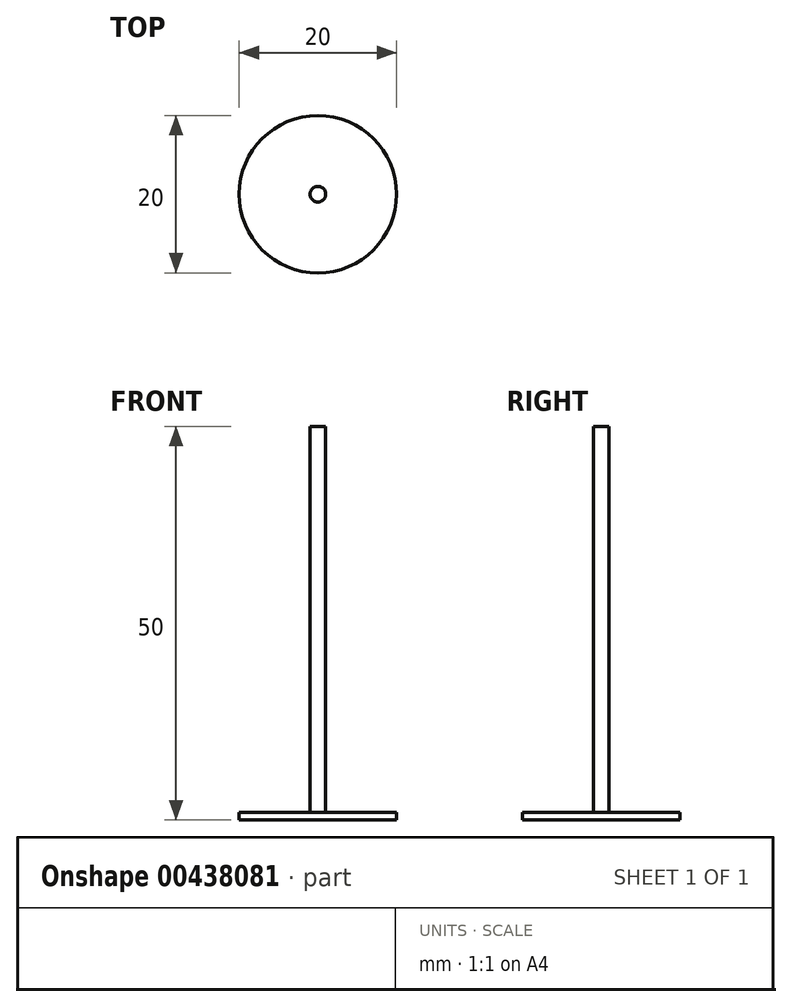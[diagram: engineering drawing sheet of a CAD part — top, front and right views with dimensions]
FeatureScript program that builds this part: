
annotation { "Feature Type Name" : "Feature", "Feature Type Description" : "" }
export const myFeature = defineFeature(function(context is Context, id is Id, definition is map)
    precondition{}
    {
        {
            var Q0;
            Q0=qCreatedBy(makeId("Top.planeOp"),FACE);
            var sketch = newSketch(context, id + "F0", { "sketchPlane" : qUnion([Q0])});
            skCircle(sketch, "E0", {"center": v(0, 0) * mm, "radius": 10 * mm});
            skSolve(sketch);
        }
        {
            var Q0;
            Q0=qSketchRegion(id+"F0",true);
            extrude(context, id + "F1", {"entities" : qUnion([Q0]), "depth" : 1 * mm});
        }
        {
            var Q0;
            Q0=qCreatedBy(makeId("Top.planeOp"),FACE);
            var sketch = newSketch(context, id + "F2", { "sketchPlane" : qUnion([Q0])});
            skCircle(sketch, "E1", {"center": v(0, 0) * mm, "radius": 1 * mm});
            skSolve(sketch);
        }
        {
            var Q0;
            Q0=qSketchRegion(id+"F2",true);
            extrude(context, id + "F3", {"entities" : qUnion([Q0]), "operationType" : NewBodyOperationType.ADD, "depth" : 50 * mm});
        }
    });
